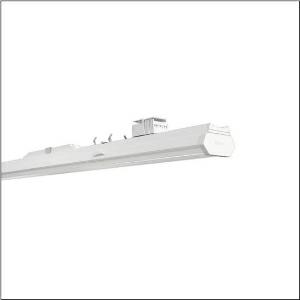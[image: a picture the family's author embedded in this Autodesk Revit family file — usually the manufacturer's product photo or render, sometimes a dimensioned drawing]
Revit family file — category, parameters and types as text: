
# Revit family: licross_r__11_protected_mo_51tp11cn58xf_4d9e
name_source: partatom
category: Lighting Fixtures
units: mm (PartAtom-declared; Revit-internal decimal feet)

## family parameters
Cut with Voids When Loaded = No
Host = Face
Light Source = No
Part Type = Normal
Room Calculation Point = No
Round Connector Dimension = Use Diameter
Shared = No

## types (1)
- --- (1 x LED, 8150 lm, 49 W, 5000K)
    Apparent Load = 49 VA
    CIE Flux Codes = 83 94 98 100 100
    Color Rendering = 80
    Color Temperature = 5000K
    Default Elevation = 1800 mm
    Description = Licross® 11 Protected MOluminaire insert, length: 1.500mm, width: 90mm, height: 101mm, LED rated luminous flux: 8.150lm, light colour: 850, control gear: ON/OFF Multilumen, CLOi, control gear: ECG Multilumen, with plug, 3-pole, with phase selection, mains connection: 220..240V, AC, 50/60Hz, halogen-free wiring, primary optical cover: cover, of PMMA, light emission: direct with ceiling illumination distribution, protection rating (complete): IP64, insulation class (complete): insulation class I (protective earthing), certification: CE, ENEC, VDE, protection symbol: D if used in an environment with conductive dust loads with corresponding accessories, permissible ambient temperature for indoor applications: -35..+40°C, corresponds to IFS (International Featured Standards) requirements for safety and quality in the food industry, reducing of maximum allowable ambient temperature of 5°C with ceiling mounting, packaging unit: 1 piece
    Height = 92 mm
    Lamp = 1 x LED
    Lamp Light Flux = 8150 lm
    Lamp Power = 49 W
    Lamp count = 1
    Length = 1500 mm
    Luminous efficacy = 166 lm/W
    Manufacturer = Siteco
    ModVariant = No
    Model = 51TP11CN58XF
    Mounting Place = Ceiling
    Mounting Type = Pendant
    Number of Poles = 1
    OnlyDefault = Yes
    Power Factor = 1
    Product Name = Licross® 11 Protected MO
    Product group = luminaire insert
    ProductGroupID = 902
    Protection Class = Protection class I
    Protection Degree = IP 64
    RLX_Detail_Level = 1
    RlxData = <blob elided: 21629 chars, md5=2d01eab7>
    Socket = socket
    Standby Power = 0 W
    System Light Flux = 8150 lm
    System Power = 49 W
    Type Comments = factory setting: luminous flux: 100 % | (A | C | E) | 111 mA
    Type Image = l_1256148.jpg
    URL = http://relux.com
    VarID = @adj_137661
    Voltage = 0 V
    Weight = 0.00 kg
    Width = 88 mm

## geometry (parser evidence)
native form markers: Blend x4, Sweep x9
no freeform markers — native parametric forms only
